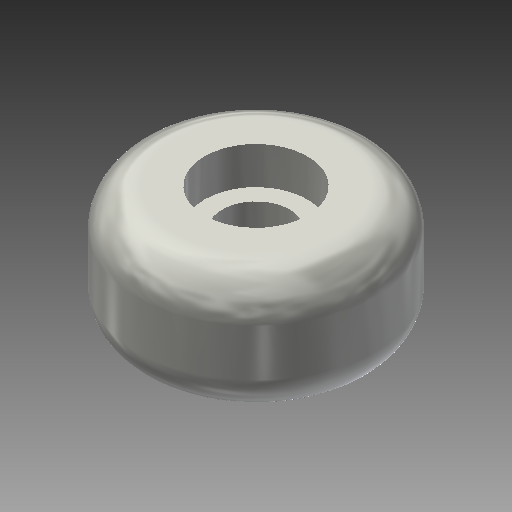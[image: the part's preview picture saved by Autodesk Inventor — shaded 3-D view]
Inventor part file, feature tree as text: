
AUTODESK INVENTOR PART (.ipt)
format: ipt  version: 2019 (Build 230136000, 136)  size: 180,224 bytes
history: native  units: mm
features: revolve x1, fillet x1, sketch x1
ambient origin geometry x8: Origin, YZ Plane, XZ Plane, XY Plane, X Axis, Y Axis, Z Axis, Center Point
bodies: Body1 (feature_tree)
feature tree (3):
  revolve  "Rivoluzione2"
  fillet  "Raccordo2"  Radius=7.25mm
  sketch  "Schizzo1"
